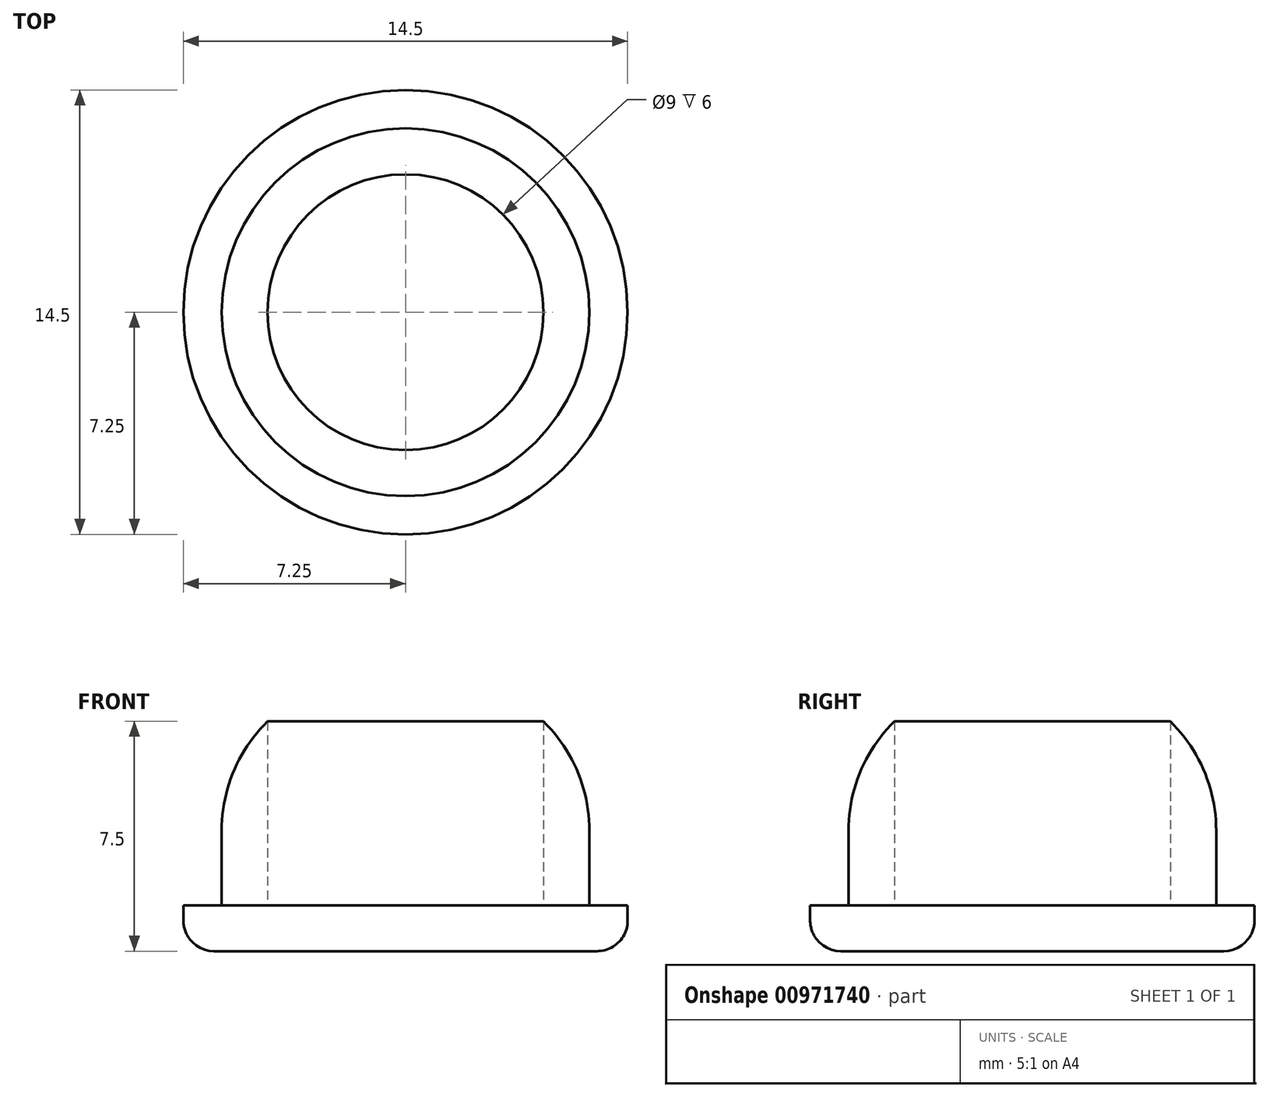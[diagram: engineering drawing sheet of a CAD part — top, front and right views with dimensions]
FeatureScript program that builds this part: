
annotation { "Feature Type Name" : "Feature", "Feature Type Description" : "" }
export const myFeature = defineFeature(function(context is Context, id is Id, definition is map)
    precondition{}
    {
        {
            var Q0;
            Q0=qCreatedBy(makeId("Top.planeOp"),FACE);
            var sketch = newSketch(context, id + "F0", { "sketchPlane" : qUnion([Q0])});
            skCircle(sketch, "E0", {"center": v(0, 0) * mm, "radius": 7.25 * mm});
            skSolve(sketch);
        }
        {
            var Q0;
            Q0=makeQuery(id+"F0.imprint","IMPRINT",FACE,{"disambiguationData":[TD([[makeQuery(id+"F0.imprint","IMPRINT",EDGE,{"derivedFrom":sQuery(id+"F0.wireOp",EDGE,"E0")}),1.0]])]});
            extrude(context, id + "F1", {"entities" : qUnion([Q0]), "oppositeDirection" : true, "depth" : 1.5 * mm, "offsetDistance" : 25 * mm});
        }
        {
            var Q0;
            Q0=makeQuery(id+"F1.opExtrude","CAP_FACE",FACE,{"disambiguationData":[OSD([sQuery(id+"F0.wireOp",EDGE,"E0")])],"isStart":true});
            var sketch = newSketch(context, id + "F2", { "sketchPlane" : qUnion([Q0])});
            skCircle(sketch, "E1", {"center": v(0, 0) * mm, "radius": 6 * mm});
            skSolve(sketch);
        }
        {
            var Q0;
            Q0=makeQuery(id+"F2.imprint","IMPRINT",FACE,{"disambiguationData":[TD([[makeQuery(id+"F2.imprint","IMPRINT",EDGE,{"derivedFrom":sQuery(id+"F2.wireOp",EDGE,"E1")}),1.0]])]});
            extrude(context, id + "F3", {"entities" : qUnion([Q0]), "operationType" : NewBodyOperationType.ADD, "depth" : 6 * mm, "offsetDistance" : 25 * mm});
        }
        {
            var Q0;
            Q0=makeQuery(id+"F3.opExtrude","CAP_FACE",FACE,{"disambiguationData":[OSD([sQuery(id+"F2.wireOp",EDGE,"E1")])],"isStart":false});
            shell(context, id + "F4", {"entities" : qUnion([Q0]), "thickness" : 1.5 * mm});
        }
        {
            var Q0;
            Q0=makeQuery(id+"F1.opExtrude","CAP_EDGE",EDGE,{"disambiguationData":[OSD([sQuery(id+"F0.wireOp",EDGE,"E0")])],"isStart":false});
            fillet(context, id + "F5", {"entities" : qUnion([Q0]), "radius" : 1 * mm, "tangentPropagation" : true, "allowEdgeOverflow" : false});
        }
        {
            var Q0;
            Q0=makeQuery(id+"F3.opExtrude","CAP_EDGE",EDGE,{"disambiguationData":[OSD([sQuery(id+"F2.wireOp",EDGE,"E1")])],"isStart":false});
            fillet(context, id + "F6", {"entities" : qUnion([Q0]), "radius" : 5 * mm, "tangentPropagation" : true, "allowEdgeOverflow" : false});
        }
    });
